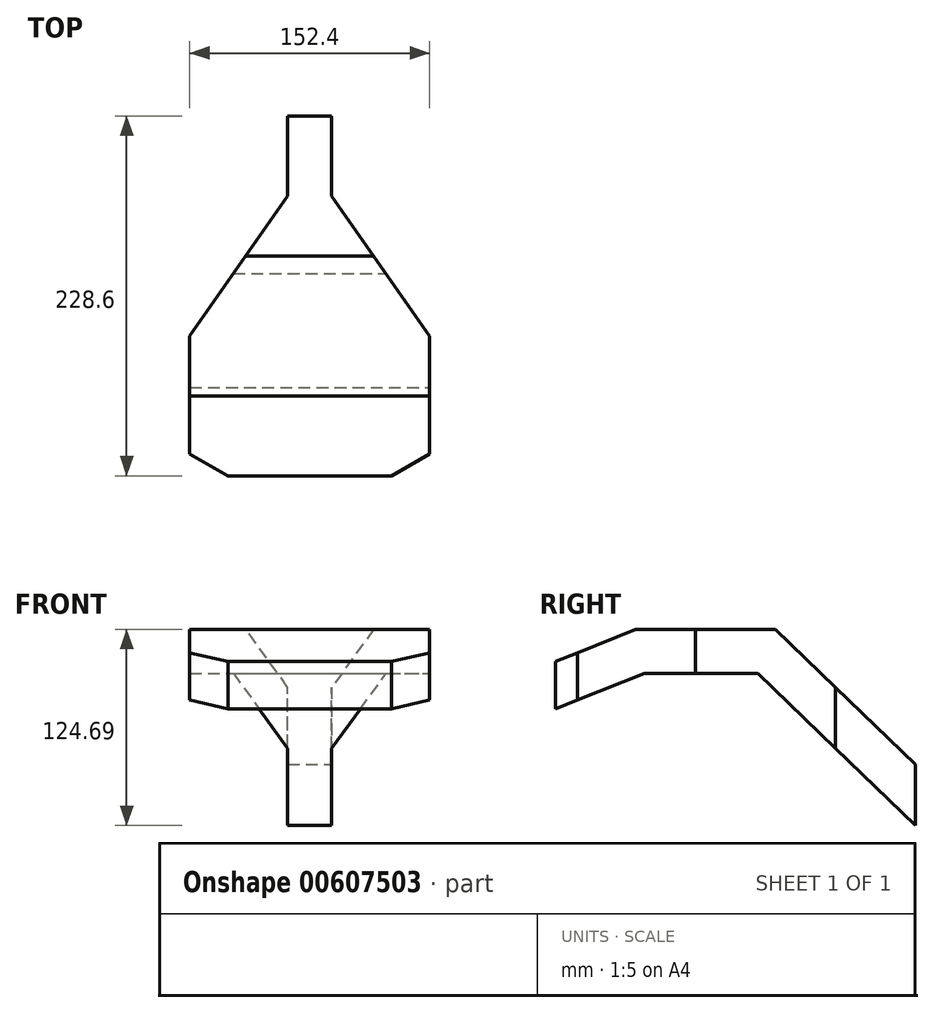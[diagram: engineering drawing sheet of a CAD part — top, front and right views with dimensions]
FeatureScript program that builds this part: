
annotation { "Feature Type Name" : "Feature", "Feature Type Description" : "" }
export const myFeature = defineFeature(function(context is Context, id is Id, definition is map)
    precondition{}
    {
        {
            var Q0;
            Q0=qCreatedBy(makeId("Top.planeOp"),FACE);
            var sketch = newSketch(context, id + "F0", { "sketchPlane" : qUnion([Q0])});
            skLineSegment(sketch, "E0", {"start": v(13.97, 88.9) * mm, "end": v(76.2, 0) * mm});
            skLineSegment(sketch, "E1", {"start": v(76.2, 0) * mm, "end": v(76.2, -74.93) * mm});
            skLineSegment(sketch, "E2", {"start": v(76.2, -74.93) * mm, "end": v(52, -88.9) * mm});
            skLineSegment(sketch, "E3", {"start": v(52, -88.9) * mm, "end": v(-52, -88.9) * mm});
            skLineSegment(sketch, "E4", {"start": v(-52, -88.9) * mm, "end": v(-76.2, -74.93) * mm});
            skLineSegment(sketch, "E5", {"start": v(-76.2, -74.93) * mm, "end": v(-76.2, 0) * mm});
            skLineSegment(sketch, "E6", {"start": v(-76.2, 0) * mm, "end": v(-13.97, 88.9) * mm});
            skLineSegment(sketch, "E7", {"start": v(-13.97, 88.9) * mm, "end": v(-13.97, 139.7) * mm});
            skLineSegment(sketch, "E8", {"start": v(-13.97, 139.7) * mm, "end": v(13.97, 139.7) * mm});
            skLineSegment(sketch, "E9", {"start": v(13.97, 139.7) * mm, "end": v(13.97, 88.9) * mm});
            skLineSegment(sketch, "E10", {"start": v(0, 139.7) * mm, "end": v(0, -88.9) * mm, "construction": true});
            skLineSegment(sketch, "E11", {"start": v(-13.97, 88.9) * mm, "end": v(13.97, 88.9) * mm, "construction": true});
            skSolve(sketch);
        }
        {
            var Q0;
            Q0 = qSketchRegion(id + "F0", true);
            extrude(context, id + "F1", {"entities" : qUnion([Q0]), "oppositeDirection" : true, "depth" : 127 * mm, "offsetDistance" : 25.4 * mm});
        }
        {
            var Q0;
            Q0=makeQuery(id+"F1.opExtrude","SWEPT_FACE",FACE,{"disambiguationData":[OSD([sQuery(id+"F0.wireOp",EDGE,"E1")])]});
            var sketch = newSketch(context, id + "F2", { "sketchPlane" : qUnion([Q0])});
            skLineSegment(sketch, "E12", {"start": v(-88.9, 0) * mm, "end": v(139.7, 0) * mm, "construction": true});
            skPoint(sketch, "E12.startSnap0", {"position": v(-37.47, 0) * mm});
            skLineSegment(sketch, "E13", {"start": v(0, 0) * mm, "end": v(-38.1, 0) * mm});
            skLineSegment(sketch, "E14", {"start": v(-38.1, 0) * mm, "end": v(-88.9, -20.52) * mm});
            skLineSegment(sketch, "E15", {"start": v(-88.9, -20.52) * mm, "end": v(-88.9, -50.66) * mm});
            skLineSegment(sketch, "E16", {"start": v(-88.9, -50.66) * mm, "end": v(-32.67, -27.94) * mm});
            skLineSegment(sketch, "E17", {"start": v(-32.67, -27.94) * mm, "end": v(39.51, -27.94) * mm});
            skLineSegment(sketch, "E18", {"start": v(39.51, -27.94) * mm, "end": v(139.7, -124.7) * mm});
            skLineSegment(sketch, "E19", {"start": v(139.7, -124.7) * mm, "end": v(139.7, -85.85) * mm});
            skLineSegment(sketch, "E20", {"start": v(139.7, -85.85) * mm, "end": v(50.8, 0) * mm});
            skLineSegment(sketch, "E21", {"start": v(50.8, 0) * mm, "end": v(0, 0) * mm});
            skSolve(sketch);
        }
        {
            var Q0;
            Q0 = qSketchRegion(id + "F2", true);
            extrude(context, id + "F3", {"entities" : qUnion([Q0]), "operationType" : NewBodyOperationType.INTERSECT, "endBound" : BoundingType.THROUGH_ALL, "oppositeDirection" : true, "depth" : 25.4 * mm, "offsetDistance" : 25.4 * mm});
        }
    });
